# Revit family: DCS_Revit_18_ADR2-24_Storage_593510A
name_source: partatom
category: Specialty Equipment
revit_build: Autodesk Revit 2018 (Build: 20170223_1515(x64)
units: mm (PartAtom-declared; Revit-internal decimal feet)

## family parameters
Always vertical = Yes
Cut with Voids When Loaded = Yes
OmniClass Number = 23.40.40.14.17.21
OmniClass Title = Grills
Part Type = Normal
Room Calculation Point = No
Round Connector Dimension = Use Diameter
Shared = No
Work Plane-Based = No

## types (1)
- ADR2-24
    Cavity - Depth = 597 mm
    Cavity - Height = 508 mm
    Cavity - Width = 560 mm  [stored 1.83727 ft]
    Chassis - Depth = 595 mm  [stored 1.9521 ft]
    Chassis - Height = 507 mm  [stored 1.66339 ft]
    Chassis - Width = 559 mm  [stored 1.83399 ft]
    Description = 24" Access Drawers Built-in
    Manufacturer = Fisher & Paykel
    Material - Body = DCS - Stainless Steel
    Material - Handle = DCS - Aluminium
    Model = ADR2-24
    Product - Depth = 676 mm  [stored 2.21785 ft]
    Product - Height = 556 mm  [stored 1.82415 ft]
    Product - Width = 610 mm  [stored 2.00131 ft]
    URL = www.dcsappliances.com
    Visibility - Clearance Required = Yes

note: [stored X ft] marks values corroborated as IEEE doubles in the binary element streams (Revit-internal decimal feet)

## geometry (parser evidence)
native form markers: Sweep x3
no freeform markers — native parametric forms only
